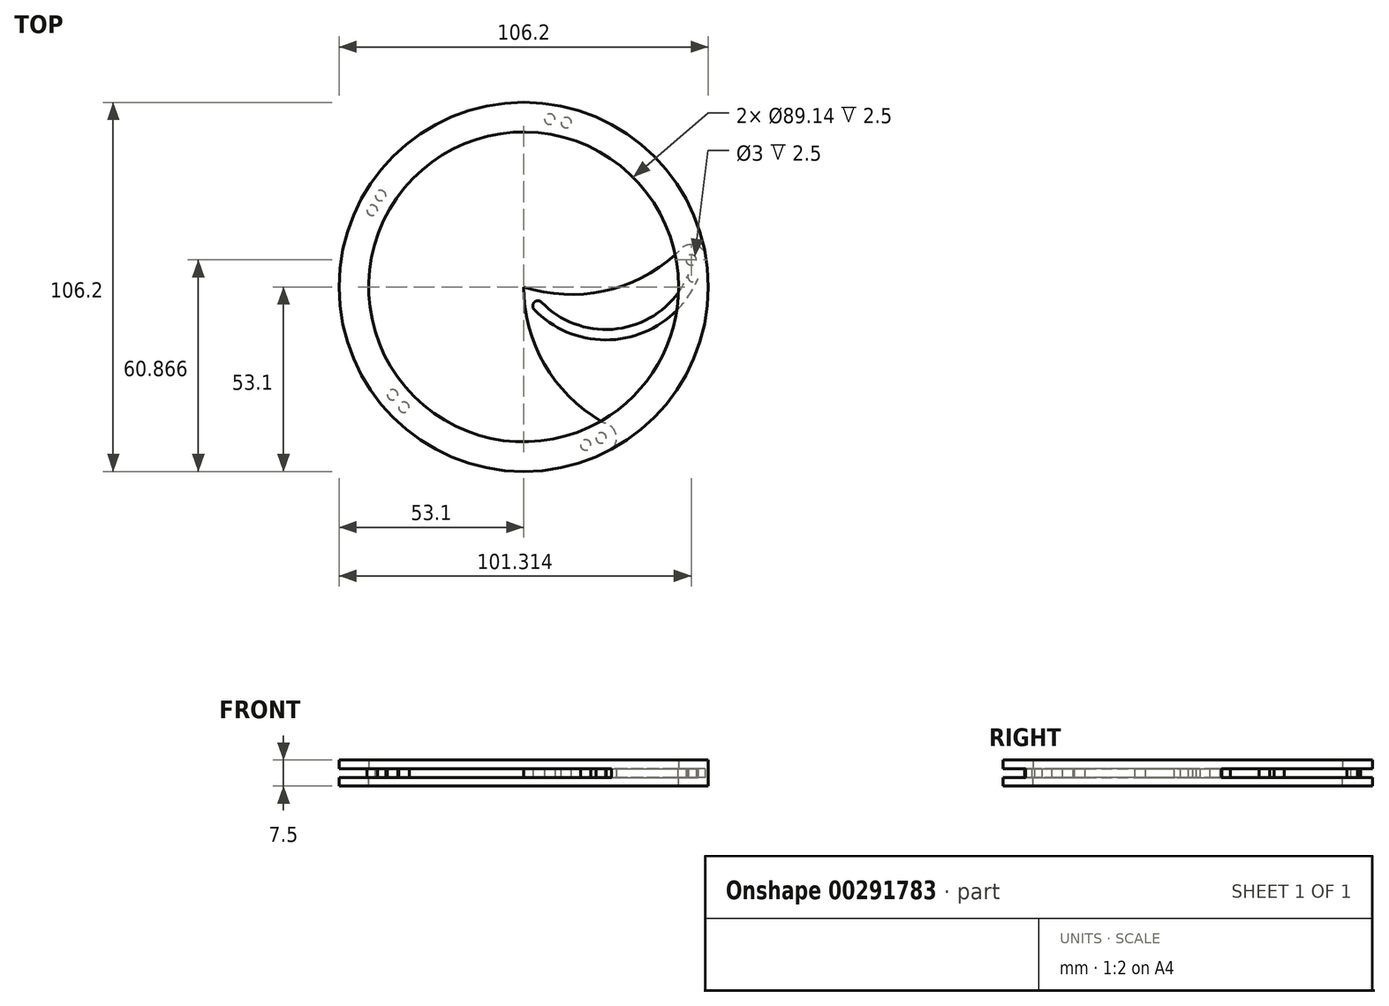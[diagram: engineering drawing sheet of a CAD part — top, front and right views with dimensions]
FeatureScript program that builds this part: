
annotation { "Feature Type Name" : "Feature", "Feature Type Description" : "" }
export const myFeature = defineFeature(function(context is Context, id is Id, definition is map)
    precondition{}
    {
        {
            assignVariable(context, id + "F0", {"name" : "plaat", "anyValue" : 2.5});
        }
        {
            var Q0;
            Q0=qCreatedBy(makeId("Top.planeOp"),FACE);
            var sketch = newSketch(context, id + "F1", { "sketchPlane" : qUnion([Q0])});
            skCircle(sketch, "E0", {"center": v(0, 0) * mm, "radius": 44.57 * mm, "construction": true});
            skLineSegment(sketch, "E1", {"start": v(0, 0) * mm, "end": v(44.57, 0) * mm, "construction": true});
            skLineSegment(sketch, "E2", {"start": v(0, 0) * mm, "end": v(13.77, 42.39) * mm, "construction": true});
            skArc(sketch, "E3", {"start": v(0, 0) * mm, "mid": v(23.04, -1.2) * mm, "end": v(43.6, 9.27) * mm});
            skArc(sketch, "E4.trimOffspring", {"start": v(0, 0) * mm, "mid": v(5.97, -22.29) * mm, "end": v(22.29, -38.6) * mm});
            skLineSegment(sketch, "E5", {"start": v(13.77, 42.39) * mm, "end": v(44.57, 0) * mm, "construction": true});
            skLineSegment(sketch, "E6", {"start": v(6.89, 21.2) * mm, "end": v(48.21, 7.77) * mm, "construction": true});
            skCircle(sketch, "E7", {"center": v(0, 0) * mm, "radius": 48.84 * mm, "construction": true});
            skCircle(sketch, "E8", {"center": v(48.21, 7.77) * mm, "radius": 48.84 * mm, "construction": true});
            skCircle(sketch, "E9", {"center": v(0, 0) * mm, "radius": 53.1 * mm});
            skLineSegment(sketch, "E10", {"start": v(44.57, 0) * mm, "end": v(48.84, 0) * mm});
            skLineSegment(sketch, "E11", {"start": v(53.1, 0) * mm, "end": v(48.84, 0) * mm});
            skCircle(sketch, "E12", {"center": v(48.21, 7.77) * mm, "radius": 4.86 * mm, "construction": true});
            skPoint(sketch, "E13", {"position": v(48.75, 2.94) * mm});
            skCircle(sketch, "E14", {"center": v(13.77, 42.39) * mm, "radius": 52.72 * mm, "construction": true});
            skCircle(sketch, "E15", {"center": v(13.77, 42.39) * mm, "radius": 48.84 * mm, "construction": true});
            skArc(sketch, "E16", {"start": v(4.11, -5.48) * mm, "mid": v(28.7, -13.28) * mm, "end": v(48.75, 2.94) * mm, "construction": true});
            skPoint(sketch, "E16.second.point", {"position": v(4.11, -5.48) * mm});
            skArc(sketch, "E17.0.startCap", {"start": v(3.04, -6.53) * mm, "mid": v(3.07, -4.4) * mm, "end": v(5.19, -4.44) * mm});
            skArc(sketch, "E17.0.endCap", {"start": v(47.36, 3.52) * mm, "mid": v(49.33, 4.32) * mm, "end": v(50.13, 2.36) * mm});
            skArc(sketch, "E17.0.left", {"start": v(5.19, -4.44) * mm, "mid": v(28.42, -11.8) * mm, "end": v(47.36, 3.52) * mm});
            skArc(sketch, "E17.0.right", {"start": v(3.04, -6.53) * mm, "mid": v(28.97, -14.75) * mm, "end": v(50.13, 2.36) * mm});
            skCircle(sketch, "E18", {"center": v(48.21, 7.77) * mm, "radius": 1.5 * mm});
            skCircle(sketch, "E19.1.0", {"center": v(7.51, 48.25) * mm, "radius": 48.84 * mm, "construction": true});
            skCircle(sketch, "E19.2.0", {"center": v(-43.57, 22.06) * mm, "radius": 48.84 * mm, "construction": true});
            skCircle(sketch, "E19.3.0", {"center": v(-34.44, -34.62) * mm, "radius": 48.84 * mm, "construction": true});
            skCircle(sketch, "E19.4.0", {"center": v(22.29, -43.45) * mm, "radius": 48.84 * mm, "construction": true});
            skLineSegment(sketch, "E20", {"start": v(0, 0) * mm, "end": v(48.21, 7.77) * mm, "construction": true});
            skLineSegment(sketch, "E21", {"start": v(43.6, 9.27) * mm, "end": v(44.37, 9.96) * mm});
            skArc(sketch, "E22.trimOffspring", {"start": v(52.6, 7.21) * mm, "mid": v(49.61, 11.97) * mm, "end": v(44.37, 9.96) * mm});
            skLineSegment(sketch, "E23.1.0", {"start": v(4.66, 44.33) * mm, "end": v(4.24, 45.27) * mm});
            skArc(sketch, "E23.1.1", {"start": v(9.4, 52.26) * mm, "mid": v(3.95, 50.88) * mm, "end": v(4.24, 45.27) * mm});
            skLineSegment(sketch, "E23.2.0", {"start": v(-40.72, 18.13) * mm, "end": v(-41.75, 18.02) * mm});
            skArc(sketch, "E23.2.1", {"start": v(-46.8, 25.09) * mm, "mid": v(-47.17, 19.48) * mm, "end": v(-41.75, 18.02) * mm});
            skLineSegment(sketch, "E23.3.0", {"start": v(-29.82, -33.12) * mm, "end": v(-30.04, -34.14) * mm});
            skArc(sketch, "E23.3.1", {"start": v(-38.32, -36.76) * mm, "mid": v(-33.1, -38.84) * mm, "end": v(-30.04, -34.14) * mm});
            skLineSegment(sketch, "E23.4.0", {"start": v(22.29, -38.6) * mm, "end": v(23.18, -39.12) * mm});
            skArc(sketch, "E23.4.1", {"start": v(23.12, -47.8) * mm, "mid": v(26.71, -43.49) * mm, "end": v(23.18, -39.12) * mm});
            skCircle(sketch, "E24", {"center": v(48.75, 2.94) * mm, "radius": 1.5 * mm});
            skSolve(sketch);
        }
        {
            var Q0;
            Q0=makeQuery(id+"F1.imprint","IMPRINT",FACE,{"disambiguationData":[TD([[makeQuery(id+"F1.imprint","IMPRINT",EDGE,{"derivedFrom":sQuery(id+"F1.wireOp",EDGE,"E3")}),-1.0]])]});
            extrude(context, id + "F2", {"entities" : qUnion([Q0]), "depth" : (getVariable(context, 'plaat')) * mm});
        }
        {
            var Q0;
            Q0=qCreatedBy(makeId("Top.planeOp"),FACE);
            var sketch = newSketch(context, id + "F3", { "sketchPlane" : qUnion([Q0])});
            skCircle(sketch, "E25.0", {"center": v(0, 0) * mm, "radius": 44.57 * mm});
            skCircle(sketch, "E26.0", {"center": v(0, 0) * mm, "radius": 53.1 * mm});
            skCircle(sketch, "E27.0", {"center": v(48.21, 7.77) * mm, "radius": 1.5 * mm});
            skCircle(sketch, "E28.1.0", {"center": v(7.51, 48.25) * mm, "radius": 1.5 * mm});
            skCircle(sketch, "E28.2.0", {"center": v(-43.57, 22.06) * mm, "radius": 1.5 * mm});
            skCircle(sketch, "E28.3.0", {"center": v(-34.44, -34.62) * mm, "radius": 1.5 * mm});
            skCircle(sketch, "E28.4.0", {"center": v(22.29, -43.45) * mm, "radius": 1.5 * mm});
            skSolve(sketch);
        }
        {
            var Q0;
            Q0=makeQuery(id+"F3.imprint","IMPRINT",FACE,{"disambiguationData":[TD([[makeQuery(id+"F3.imprint","IMPRINT",EDGE,{"derivedFrom":sQuery(id+"F3.wireOp",EDGE,"E25.0")}),-1.0]])]});
            var Q1;
            Q1=makeQuery(id+"F3.imprint","IMPRINT",FACE,{"disambiguationData":[TD([[makeQuery(id+"F3.imprint","IMPRINT",EDGE,{"derivedFrom":sQuery(id+"F3.wireOp",EDGE,"E28.4.0")}),1.0]])]});
            var Q2;
            Q2=makeQuery(id+"F3.imprint","IMPRINT",FACE,{"disambiguationData":[TD([[makeQuery(id+"F3.imprint","IMPRINT",EDGE,{"derivedFrom":sQuery(id+"F3.wireOp",EDGE,"E27.0")}),1.0]])]});
            var Q3;
            Q3=makeQuery(id+"F3.imprint","IMPRINT",FACE,{"disambiguationData":[TD([[makeQuery(id+"F3.imprint","IMPRINT",EDGE,{"derivedFrom":sQuery(id+"F3.wireOp",EDGE,"E28.1.0")}),1.0]])]});
            var Q4;
            Q4=makeQuery(id+"F3.imprint","IMPRINT",FACE,{"disambiguationData":[TD([[makeQuery(id+"F3.imprint","IMPRINT",EDGE,{"derivedFrom":sQuery(id+"F3.wireOp",EDGE,"E28.2.0")}),1.0]])]});
            var Q5;
            Q5=makeQuery(id+"F3.imprint","IMPRINT",FACE,{"disambiguationData":[TD([[makeQuery(id+"F3.imprint","IMPRINT",EDGE,{"derivedFrom":sQuery(id+"F3.wireOp",EDGE,"E28.3.0")}),1.0]])]});
            extrude(context, id + "F4", {"entities" : qUnion([Q0, Q1, Q2, Q3, Q4, Q5]), "oppositeDirection" : true, "depth" : (getVariable(context, 'plaat')) * mm});
        }
        {
            var Q0;
            Q0=makeQuery(id+"F3.imprint","IMPRINT",FACE,{"disambiguationData":[TD([[makeQuery(id+"F3.imprint","IMPRINT",EDGE,{"derivedFrom":sQuery(id+"F3.wireOp",EDGE,"E28.1.0")}),1.0]])]});
            var Q1;
            Q1=makeQuery(id+"F3.imprint","IMPRINT",FACE,{"disambiguationData":[TD([[makeQuery(id+"F3.imprint","IMPRINT",EDGE,{"derivedFrom":sQuery(id+"F3.wireOp",EDGE,"E28.2.0")}),1.0]])]});
            var Q2;
            Q2=makeQuery(id+"F3.imprint","IMPRINT",FACE,{"disambiguationData":[TD([[makeQuery(id+"F3.imprint","IMPRINT",EDGE,{"derivedFrom":sQuery(id+"F3.wireOp",EDGE,"E28.3.0")}),1.0]])]});
            var Q3;
            Q3=makeQuery(id+"F3.imprint","IMPRINT",FACE,{"disambiguationData":[TD([[makeQuery(id+"F3.imprint","IMPRINT",EDGE,{"derivedFrom":sQuery(id+"F3.wireOp",EDGE,"E28.4.0")}),1.0]])]});
            var Q4;
            Q4=makeQuery(id+"F3.imprint","IMPRINT",FACE,{"disambiguationData":[TD([[makeQuery(id+"F3.imprint","IMPRINT",EDGE,{"derivedFrom":sQuery(id+"F3.wireOp",EDGE,"E27.0")}),1.0]])]});
            var Q5;
            Q5=sQuery(id+"F3.wireOp",EDGE,"E28.4.0");
            var Q6;
            Q6=sQuery(id+"F3.wireOp",EDGE,"E27.0");
            var Q7;
            Q7=sQuery(id+"F3.wireOp",EDGE,"E28.2.0");
            var Q8;
            Q8=sQuery(id+"F3.wireOp",EDGE,"E28.1.0");
            var Q9;
            Q9=sQuery(id+"F3.wireOp",EDGE,"E28.3.0");
            extrude(context, id + "F5", {"entities" : qUnion([Q0, Q1, Q2, Q3, Q4]), "surfaceEntities" : qUnion([Q5, Q6, Q7, Q8, Q9]), "depth" : (getVariable(context, 'plaat')) * mm});
        }
        {
            var Q0;
            Q0=makeQuery(id+"F2.opExtrude","CAP_FACE",FACE,{"disambiguationData":[OSD([sQuery(id+"F1.wireOp",EDGE,"E3"),sQuery(id+"F1.wireOp",EDGE,"E4.trimOffspring"),sQuery(id+"F1.wireOp",EDGE,"E9"),sQuery(id+"F1.wireOp",EDGE,"E17.0.startCap"),sQuery(id+"F1.wireOp",EDGE,"E17.0.left"),sQuery(id+"F1.wireOp",EDGE,"E17.0.right"),sQuery(id+"F1.wireOp",EDGE,"E18"),sQuery(id+"F1.wireOp",EDGE,"E21"),sQuery(id+"F1.wireOp",EDGE,"E22.trimOffspring"),sQuery(id+"F1.wireOp",EDGE,"E23.4.0"),sQuery(id+"F1.wireOp",EDGE,"E23.4.1"),sQuery(id+"F1.wireOp",EDGE,"E24")])],"isStart":false});
            var sketch = newSketch(context, id + "F6", { "sketchPlane" : qUnion([Q0])});
            skCircle(sketch, "E29.0", {"center": v(48.75, 2.94) * mm, "radius": 1.5 * mm});
            skCircle(sketch, "E29.1", {"center": v(0, 0) * mm, "radius": 53.1 * mm});
            skCircle(sketch, "E29.2", {"center": v(0, 0) * mm, "radius": 44.57 * mm});
            skCircle(sketch, "E30.1.0", {"center": v(12.27, 47.27) * mm, "radius": 1.5 * mm});
            skCircle(sketch, "E30.2.0", {"center": v(-41.17, 26.27) * mm, "radius": 1.5 * mm});
            skCircle(sketch, "E30.3.0", {"center": v(-37.7, -31.03) * mm, "radius": 1.5 * mm});
            skCircle(sketch, "E30.4.0", {"center": v(17.86, -45.45) * mm, "radius": 1.5 * mm});
            skSolve(sketch);
        }
        {
            var Q0;
            Q0 = qSketchRegion(id + "F6", true);
            extrude(context, id + "F7", {"entities" : qUnion([Q0]), "depth" : (getVariable(context, 'plaat')) * mm});
        }
        {
            var Q0;
            Q0=makeQuery(id+"F6.imprint","IMPRINT",FACE,{"disambiguationData":[TD([[makeQuery(id+"F6.imprint","IMPRINT",EDGE,{"derivedFrom":sQuery(id+"F6.wireOp",EDGE,"E30.3.0")}),1.0]])]});
            var Q1;
            Q1=makeQuery(id+"F6.imprint","IMPRINT",FACE,{"disambiguationData":[TD([[makeQuery(id+"F6.imprint","IMPRINT",EDGE,{"derivedFrom":sQuery(id+"F6.wireOp",EDGE,"E30.2.0")}),1.0]])]});
            var Q2;
            Q2=makeQuery(id+"F6.imprint","IMPRINT",FACE,{"disambiguationData":[TD([[makeQuery(id+"F6.imprint","IMPRINT",EDGE,{"derivedFrom":sQuery(id+"F6.wireOp",EDGE,"E30.1.0")}),1.0]])]});
            var Q3;
            {var subQ0=sQuery(id+"F6.wireOp",EDGE,"E29.0");var subQ1=makeQuery(id+"F6.imprint","INTERSECT",VERTEX,{"derivedFrom":[makeQuery(id+"F2.opExtrude","CAP_EDGE",EDGE,{"disambiguationData":[OSD([sQuery(id+"F1.wireOp",EDGE,"E17.0.left")])],"isStart":false}),subQ0]});Q3=makeQuery(id+"F6.imprint","IMPRINT",FACE,{"disambiguationData":[TD([[makeQuery(id+"F6.imprint","IMPRINT",EDGE,{"disambiguationData":[TD([[subQ1,-1.0]])],"derivedFrom":subQ0}),1.0]])]});}
            var Q4;
            Q4=makeQuery(id+"F6.imprint","IMPRINT",FACE,{"disambiguationData":[TD([[makeQuery(id+"F6.imprint","IMPRINT",EDGE,{"derivedFrom":sQuery(id+"F6.wireOp",EDGE,"E30.4.0")}),1.0]])]});
            var Q5;
            Q5=makeQuery(id+"F2.opExtrude","CAP_FACE",FACE,{"disambiguationData":[OSD([sQuery(id+"F1.wireOp",EDGE,"E3"),sQuery(id+"F1.wireOp",EDGE,"E4.trimOffspring"),sQuery(id+"F1.wireOp",EDGE,"E9"),sQuery(id+"F1.wireOp",EDGE,"E17.0.startCap"),sQuery(id+"F1.wireOp",EDGE,"E17.0.left"),sQuery(id+"F1.wireOp",EDGE,"E17.0.right"),sQuery(id+"F1.wireOp",EDGE,"E18"),sQuery(id+"F1.wireOp",EDGE,"E21"),sQuery(id+"F1.wireOp",EDGE,"E22.trimOffspring"),sQuery(id+"F1.wireOp",EDGE,"E23.4.0"),sQuery(id+"F1.wireOp",EDGE,"E23.4.1"),sQuery(id+"F1.wireOp",EDGE,"E24")])],"isStart":true});
            var Q6;
            Q6=makeQuery(id+"F7.opExtrude","CAP_FACE",FACE,{"disambiguationData":[OSD([sQuery(id+"F6.wireOp",EDGE,"E29.0"),sQuery(id+"F6.wireOp",EDGE,"E29.1"),sQuery(id+"F6.wireOp",EDGE,"E29.2"),sQuery(id+"F6.wireOp",EDGE,"E30.1.0"),sQuery(id+"F6.wireOp",EDGE,"E30.2.0"),sQuery(id+"F6.wireOp",EDGE,"E30.3.0"),sQuery(id+"F6.wireOp",EDGE,"E30.4.0")])],"isStart":false});
            extrude(context, id + "F8", {"entities" : qUnion([Q0, Q1, Q2, Q3, Q4]), "operationType" : NewBodyOperationType.ADD, "endBound" : BoundingType.UP_TO_SURFACE, "oppositeDirection" : true, "endBoundEntityFace" : qUnion([Q5]), "depth" : 25 * mm, "hasSecondDirection" : true, "secondDirectionBound" : SecondDirectionBoundingType.UP_TO_SURFACE, "secondDirectionOppositeDirection" : false, "secondDirectionBoundEntityFace" : qUnion([Q6]), "secondDirectionDepth" : 25 * mm});
        }
    });
